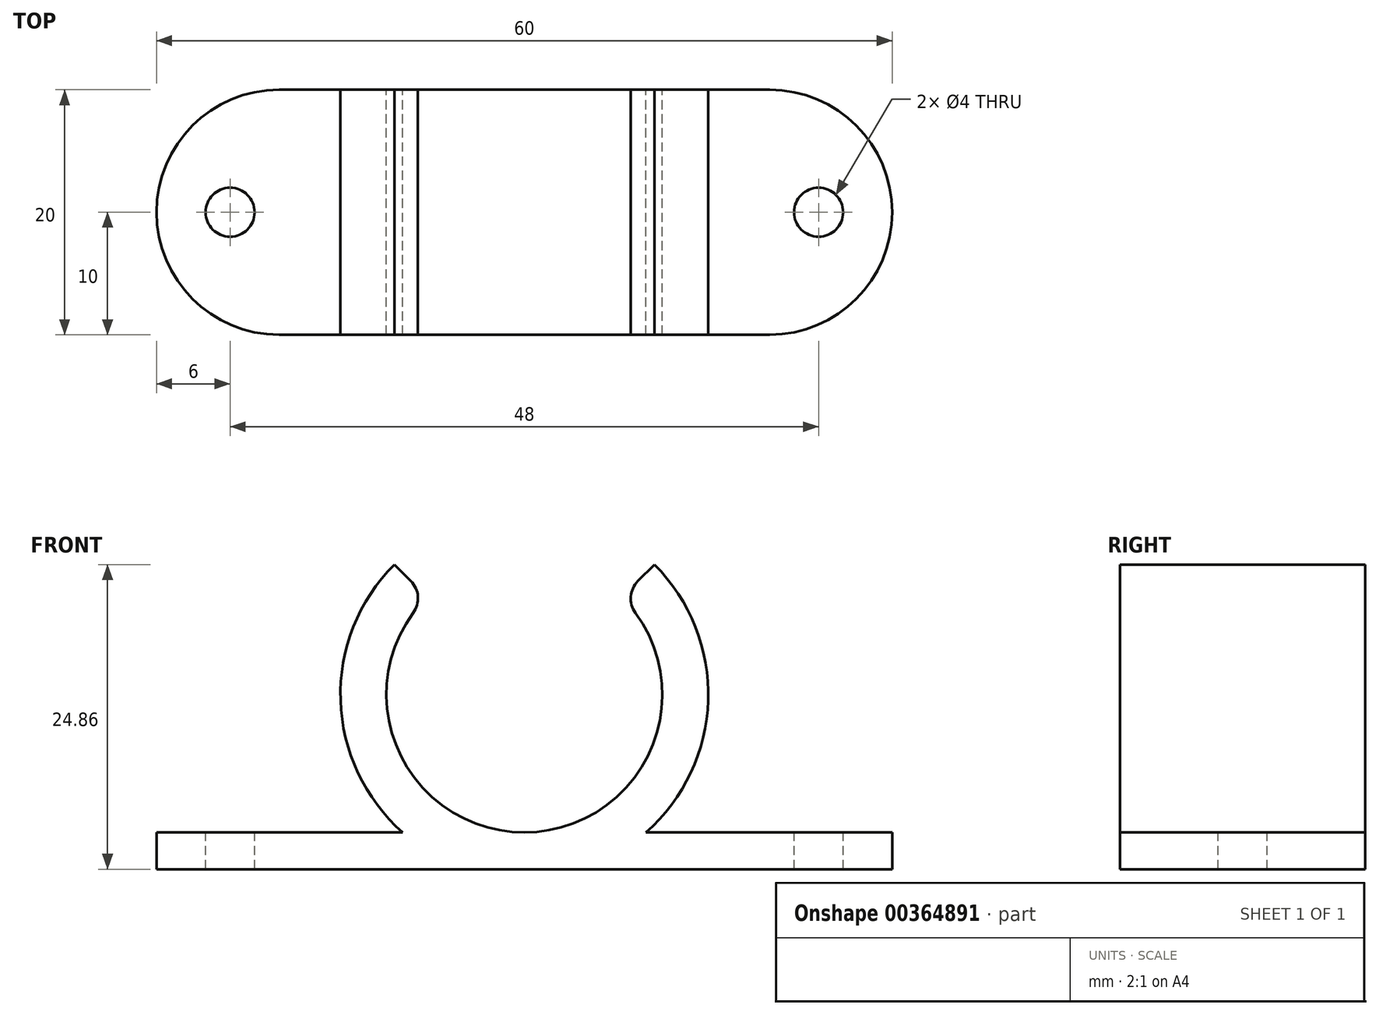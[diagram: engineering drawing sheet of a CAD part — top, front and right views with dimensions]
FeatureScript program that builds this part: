
annotation { "Feature Type Name" : "Feature", "Feature Type Description" : "" }
export const myFeature = defineFeature(function(context is Context, id is Id, definition is map)
    precondition{}
    {
        {
            var Q0;
            Q0=qCreatedBy(makeId("Front.planeOp"),FACE);
            var sketch = newSketch(context, id + "F0", { "sketchPlane" : qUnion([Q0])});
            skLineSegment(sketch, "E0.bottom", {"start": v(0, 0) * mm, "end": v(60, 0) * mm});
            skLineSegment(sketch, "E0.top", {"start": v(0, 3) * mm, "end": v(20.08, 3) * mm});
            skLineSegment(sketch, "E0.left", {"start": v(0, 0) * mm, "end": v(0, 3) * mm});
            skLineSegment(sketch, "E0.right", {"start": v(60, 0) * mm, "end": v(60, 3) * mm});
            skArc(sketch, "E1", {"start": v(22.05, 22.2) * mm, "mid": v(30, 3) * mm, "end": v(37.95, 22.2) * mm});
            skArc(sketch, "E2", {"start": v(39.92, 3) * mm, "mid": v(45, 13.78) * mm, "end": v(40.6, 24.86) * mm});
            skLineSegment(sketch, "E3.trimOffspring", {"start": v(39.92, 3) * mm, "end": v(60, 3) * mm});
            skLineSegment(sketch, "E4", {"start": v(22.05, 22.2) * mm, "end": v(19.4, 24.86) * mm});
            skLineSegment(sketch, "E5", {"start": v(37.95, 22.2) * mm, "end": v(40.6, 24.86) * mm});
            skArc(sketch, "E6.trimOffspring", {"start": v(19.4, 24.86) * mm, "mid": v(15, 13.78) * mm, "end": v(20.08, 3) * mm});
            skLineSegment(sketch, "E7.trimOffspring", {"start": v(30, 29.25) * mm, "end": v(30, 37) * mm});
            skSolve(sketch);
        }
        {
            var Q0;
            Q0 = qSketchRegion(id + "F0", true);
            extrude(context, id + "F1", {"entities" : qUnion([Q0]), "depth" : 20 * mm});
        }
        {
            var Q0;
            Q0=makeQuery(id+"F1.opExtrude","SWEPT_EDGE",EDGE,{"disambiguationData":[OSD([sQuery(id+"F0.wireOp",EDGE,"E1"),sQuery(id+"F0.wireOp",EDGE,"E4")])]});
            var Q1;
            Q1=makeQuery(id+"F1.opExtrude","SWEPT_EDGE",EDGE,{"disambiguationData":[OSD([sQuery(id+"F0.wireOp",EDGE,"E1"),sQuery(id+"F0.wireOp",EDGE,"E5")])]});
            fillet(context, id + "F2", {"entities" : qUnion([Q0, Q1]), "radius" : 2 * mm, "tangentPropagation" : true, "allowEdgeOverflow" : false});
        }
        {
            var Q0;
            Q0=makeQuery(id+"F1.opExtrude","SWEPT_FACE",FACE,{"disambiguationData":[OSD([sQuery(id+"F0.wireOp",EDGE,"E0.top")])]});
            var sketch = newSketch(context, id + "F3", { "sketchPlane" : qUnion([Q0])});
            skCircle(sketch, "E8", {"center": v(6, -10) * mm, "radius": 2 * mm});
            skCircle(sketch, "E9", {"center": v(54, -10) * mm, "radius": 2 * mm});
            skSolve(sketch);
        }
        {
            var Q0;
            Q0 = qSketchRegion(id + "F3", true);
            extrude(context, id + "F4", {"entities" : qUnion([Q0]), "operationType" : NewBodyOperationType.REMOVE, "oppositeDirection" : true, "depth" : 25 * mm});
        }
        {
            var Q0;
            Q0=makeQuery(id+"F1.opExtrude","CAP_EDGE",EDGE,{"disambiguationData":[OSD([sQuery(id+"F0.wireOp",EDGE,"E0.left")])],"isStart":true});
            var Q1;
            Q1=makeQuery(id+"F1.opExtrude","CAP_EDGE",EDGE,{"disambiguationData":[OSD([sQuery(id+"F0.wireOp",EDGE,"E0.left")])],"isStart":false});
            var Q2;
            Q2=makeQuery(id+"F1.opExtrude","CAP_EDGE",EDGE,{"disambiguationData":[OSD([sQuery(id+"F0.wireOp",EDGE,"E0.right")])],"isStart":false});
            var Q3;
            Q3=makeQuery(id+"F1.opExtrude","CAP_EDGE",EDGE,{"disambiguationData":[OSD([sQuery(id+"F0.wireOp",EDGE,"E0.right")])],"isStart":true});
            fillet(context, id + "F5", {"entities" : qUnion([Q0, Q1, Q2, Q3]), "radius" : 10 * mm, "tangentPropagation" : true, "allowEdgeOverflow" : false});
        }
    });
